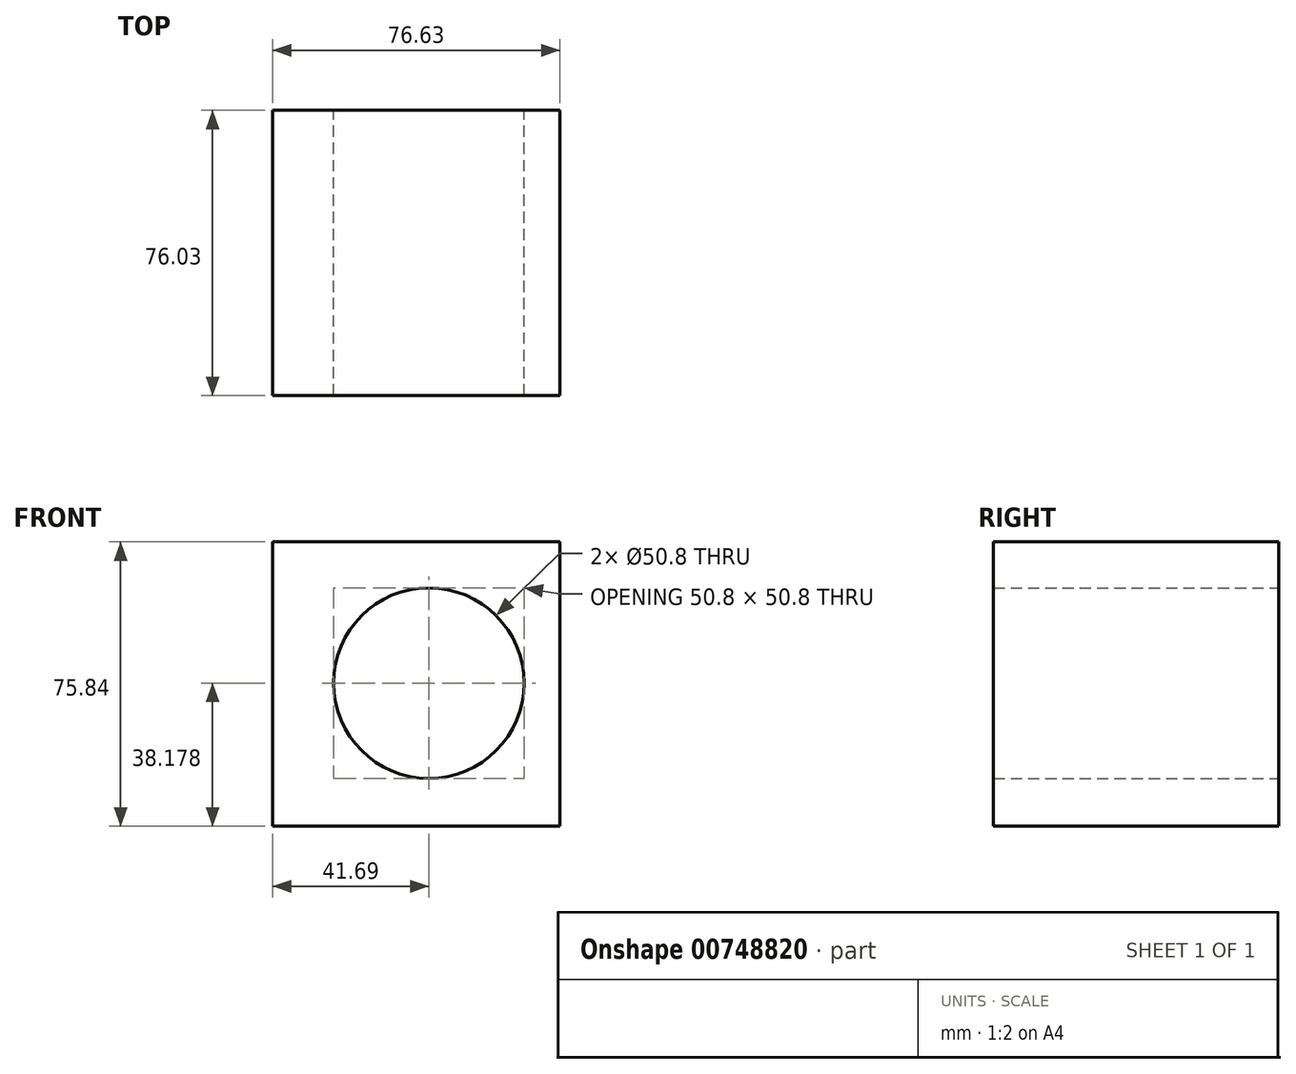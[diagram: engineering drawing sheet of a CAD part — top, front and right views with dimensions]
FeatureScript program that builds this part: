
annotation { "Feature Type Name" : "Feature", "Feature Type Description" : "" }
export const myFeature = defineFeature(function(context is Context, id is Id, definition is map)
    precondition{}
    {
        {
            var Q0;
            Q0=qCreatedBy(makeId("Front.planeOp"),FACE);
            var sketch = newSketch(context, id + "F0", { "sketchPlane" : qUnion([Q0])});
            skLineSegment(sketch, "E0", {"start": v(0, 0) * mm, "end": v(0, -75.84) * mm});
            skLineSegment(sketch, "E1", {"start": v(0, -75.84) * mm, "end": v(-76.63, -75.84) * mm});
            skLineSegment(sketch, "E2", {"start": v(-76.63, -75.84) * mm, "end": v(-76.63, 0) * mm});
            skLineSegment(sketch, "E3", {"start": v(-76.63, 0) * mm, "end": v(0, 0) * mm});
            skSolve(sketch);
        }
        {
            var Q0;
            Q0 = qSketchRegion(id + "F0", true);
            extrude(context, id + "F1", {"entities" : qUnion([Q0]), "depth" : 76.03 * mm, "offsetDistance" : 25.4 * mm});
        }
        {
            var Q0;
            Q0=qCreatedBy(makeId("Front.planeOp"),FACE);
            var sketch = newSketch(context, id + "F2", { "sketchPlane" : qUnion([Q0])});
            skPoint(sketch, "E4", {"position": v(-34.94, -37.66) * mm});
            skSolve(sketch);
        }
        {
            var Q0;
            Q0=sQuery(id+"F2.wireOp",VERTEX,"E4");
            var Q1;
            Q1=makeQuery(id+"F1.opExtrude","SWEPT_BODY",BODY,{"disambiguationData":[OSD([sQuery(id+"F0.wireOp",EDGE,"E0"),sQuery(id+"F0.wireOp",EDGE,"E1"),sQuery(id+"F0.wireOp",EDGE,"E2"),sQuery(id+"F0.wireOp",EDGE,"E3")])]});
            hole(context, id + "F3", {"style" : HoleStyle.SIMPLE, "endStyle" : HoleEndStyle.THROUGH, "oppositeDirection" : true, "holeDiameter" : 50.8 * mm, "majorDiameter" : 6.35 * mm, "isTappedThrough" : true, "tappedDepth" : 12.7 * mm, "tapClearance" : 3, "locations" : qUnion([Q0]), "scope" : qUnion([Q1])});
        }
    });
